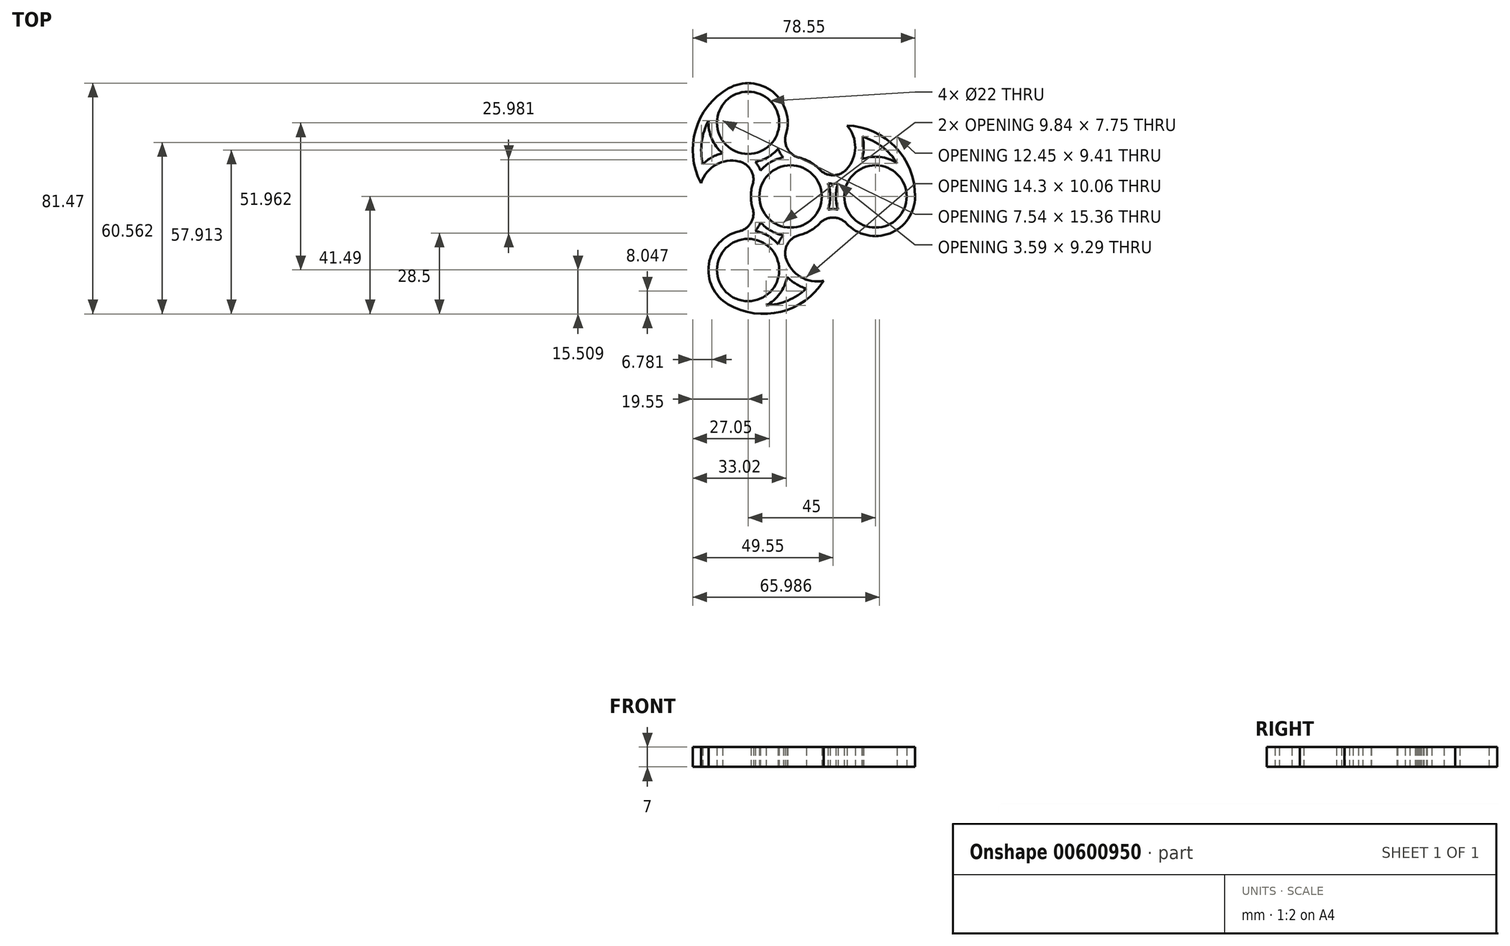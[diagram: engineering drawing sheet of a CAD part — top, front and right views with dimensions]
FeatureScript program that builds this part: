
annotation { "Feature Type Name" : "Feature", "Feature Type Description" : "" }
export const myFeature = defineFeature(function(context is Context, id is Id, definition is map)
    precondition{}
    {
        {
            var Q0;
            Q0=qCreatedBy(makeId("Top.planeOp"),FACE);
            var sketch = newSketch(context, id + "F0", { "sketchPlane" : qUnion([Q0])});
            skCircle(sketch, "E0", {"center": v(0, 0) * mm, "radius": 11 * mm});
            skCircle(sketch, "E1", {"center": v(0, 0) * mm, "radius": 30 * mm, "construction": true});
            skCircle(sketch, "E2", {"center": v(30, 0) * mm, "radius": 11 * mm});
            skArc(sketch, "E3.0", {"start": v(19.76, -9.54) * mm, "mid": v(35.1, -13.04) * mm, "end": v(44, -0.08) * mm});
            skCircle(sketch, "E4", {"center": v(0, 0) * mm, "radius": 32 * mm, "construction": true});
            skLineSegment(sketch, "E5", {"start": v(30, 0) * mm, "end": v(19.92, 25.05) * mm, "construction": true});
            skArc(sketch, "E6", {"start": v(44, -0.08) * mm, "mid": v(37.05, 17.36) * mm, "end": v(19.92, 25.05) * mm});
            skArc(sketch, "E7", {"start": v(19.76, 9.54) * mm, "mid": v(22.84, 17.26) * mm, "end": v(19.92, 25.05) * mm});
            skArc(sketch, "E8.0", {"start": v(13.2, -4.64) * mm, "mid": v(14, 0) * mm, "end": v(13.2, 4.64) * mm});
            skArc(sketch, "E9", {"start": v(10.24, 9.54) * mm, "mid": v(15, 7.47) * mm, "end": v(19.76, 9.54) * mm});
            skArc(sketch, "E10.0", {"start": v(13.2, 4.64) * mm, "mid": v(15, 4.47) * mm, "end": v(16.8, 4.64) * mm});
            skArc(sketch, "E11.MirrorCS", {"start": v(13.2, -4.64) * mm, "mid": v(15, -4.47) * mm, "end": v(16.8, -4.64) * mm});
            skArc(sketch, "E12.MirrorCS", {"start": v(10.24, -9.54) * mm, "mid": v(15, -7.47) * mm, "end": v(19.76, -9.54) * mm});
            skArc(sketch, "E13.trimOffspring", {"start": v(16.8, 4.64) * mm, "mid": v(16, 0) * mm, "end": v(16.8, -4.64) * mm});
            skArc(sketch, "E14.trimOffspring", {"start": v(10.24, 9.54) * mm, "mid": v(7, 12.12) * mm, "end": v(3.14, 13.64) * mm});
            skArc(sketch, "E15.0", {"start": v(37.66, 11.72) * mm, "mid": v(32.36, 17.54) * mm, "end": v(25.35, 21.13) * mm});
            skArc(sketch, "E16.0", {"start": v(25.21, 13.16) * mm, "mid": v(25.84, 17.13) * mm, "end": v(25.35, 21.13) * mm});
            skArc(sketch, "E17.trimOffspring", {"start": v(37.66, 11.72) * mm, "mid": v(31.6, 13.9) * mm, "end": v(25.21, 13.16) * mm});
            skArc(sketch, "E18.1.0", {"start": v(-28.98, 26.75) * mm, "mid": v(-27.85, 20.42) * mm, "end": v(-24, 15.26) * mm});
            skArc(sketch, "E18.1.1", {"start": v(-24, 15.26) * mm, "mid": v(-27.76, 13.81) * mm, "end": v(-30.97, 11.4) * mm});
            skArc(sketch, "E18.1.2", {"start": v(3.14, 13.64) * mm, "mid": v(-1.03, 16.73) * mm, "end": v(-1.61, 21.88) * mm});
            skArc(sketch, "E18.1.3", {"start": v(-2.58, 13.76) * mm, "mid": v(-3.63, 15.23) * mm, "end": v(-4.37, 16.86) * mm});
            skArc(sketch, "E18.1.4", {"start": v(-10.63, 9.12) * mm, "mid": v(-11.37, 10.75) * mm, "end": v(-12.42, 12.22) * mm});
            skArc(sketch, "E18.1.5", {"start": v(-13.39, 4.1) * mm, "mid": v(-13.97, 9.25) * mm, "end": v(-18.14, 12.34) * mm});
            skArc(sketch, "E18.1.6", {"start": v(-2.58, 13.76) * mm, "mid": v(-7, 12.12) * mm, "end": v(-10.63, 9.12) * mm});
            skArc(sketch, "E18.1.7", {"start": v(-18.14, 12.34) * mm, "mid": v(-26.37, 11.15) * mm, "end": v(-31.65, 4.73) * mm});
            skArc(sketch, "E18.1.8", {"start": v(-21.93, 38.15) * mm, "mid": v(-33.56, 23.4) * mm, "end": v(-31.65, 4.73) * mm});
            skArc(sketch, "E18.1.9", {"start": v(-1.61, 21.88) * mm, "mid": v(-6.25, 36.9) * mm, "end": v(-21.93, 38.15) * mm});
            skCircle(sketch, "E18.1.10", {"center": v(-15, 25.98) * mm, "radius": 11 * mm});
            skArc(sketch, "E18.1.11", {"start": v(-28.98, 26.75) * mm, "mid": v(-31.37, 19.25) * mm, "end": v(-30.97, 11.4) * mm});
            skArc(sketch, "E18.1.12", {"start": v(-12.42, 12.22) * mm, "mid": v(-8, 13.86) * mm, "end": v(-4.37, 16.86) * mm});
            skArc(sketch, "E18.2.0", {"start": v(-8.68, -38.47) * mm, "mid": v(-3.76, -34.32) * mm, "end": v(-1.21, -28.41) * mm});
            skArc(sketch, "E18.2.1", {"start": v(-1.21, -28.41) * mm, "mid": v(1.92, -30.94) * mm, "end": v(5.62, -32.52) * mm});
            skArc(sketch, "E18.2.2", {"start": v(-13.39, -4.1) * mm, "mid": v(-13.97, -9.25) * mm, "end": v(-18.14, -12.34) * mm});
            skArc(sketch, "E18.2.3", {"start": v(-10.63, -9.12) * mm, "mid": v(-11.37, -10.75) * mm, "end": v(-12.42, -12.22) * mm});
            skArc(sketch, "E18.2.4", {"start": v(-2.58, -13.76) * mm, "mid": v(-3.63, -15.23) * mm, "end": v(-4.37, -16.86) * mm});
            skArc(sketch, "E18.2.5", {"start": v(3.14, -13.64) * mm, "mid": v(-1.03, -16.73) * mm, "end": v(-1.61, -21.88) * mm});
            skArc(sketch, "E18.2.6", {"start": v(-10.63, -9.12) * mm, "mid": v(-7, -12.12) * mm, "end": v(-2.58, -13.76) * mm});
            skArc(sketch, "E18.2.7", {"start": v(-1.61, -21.88) * mm, "mid": v(3.53, -28.41) * mm, "end": v(11.73, -29.77) * mm});
            skArc(sketch, "E18.2.8", {"start": v(-22.07, -38.06) * mm, "mid": v(-3.49, -40.77) * mm, "end": v(11.73, -29.77) * mm});
            skArc(sketch, "E18.2.9", {"start": v(-18.14, -12.34) * mm, "mid": v(-28.84, -23.87) * mm, "end": v(-22.07, -38.06) * mm});
            skCircle(sketch, "E18.2.10", {"center": v(-15, -25.98) * mm, "radius": 11 * mm});
            skArc(sketch, "E18.2.11", {"start": v(-8.68, -38.47) * mm, "mid": v(-0.99, -36.8) * mm, "end": v(5.62, -32.52) * mm});
            skArc(sketch, "E18.2.12", {"start": v(-4.37, -16.86) * mm, "mid": v(-8, -13.86) * mm, "end": v(-12.42, -12.22) * mm});
            skArc(sketch, "E19.trimOffspring", {"start": v(-13.39, 4.1) * mm, "mid": v(-14, 0) * mm, "end": v(-13.39, -4.1) * mm});
            skArc(sketch, "E20.trimOffspring", {"start": v(3.14, -13.64) * mm, "mid": v(7, -12.12) * mm, "end": v(10.24, -9.54) * mm});
            skLineSegment(sketch, "E21", {"start": v(19.76, 9.54) * mm, "end": v(19.76, 9.54) * mm});
            skLineSegment(sketch, "E22", {"start": v(-18.14, 12.34) * mm, "end": v(-18.14, 12.34) * mm});
            skLineSegment(sketch, "E23", {"start": v(-1.61, -21.88) * mm, "end": v(-1.61, -21.88) * mm});
            skSolve(sketch);
        }
        {
            var Q0;
            Q0=makeQuery(id+"F0.imprint","IMPRINT",FACE,{"disambiguationData":[TD([[makeQuery(id+"F0.imprint","IMPRINT",EDGE,{"derivedFrom":sQuery(id+"F0.wireOp",EDGE,"E0")}),-1.0]])]});
            extrude(context, id + "F1", {"entities" : qUnion([Q0]), "endBound" : BoundingType.SYMMETRIC, "depth" : 7 * mm, "offsetDistance" : 25 * mm});
        }
    });
